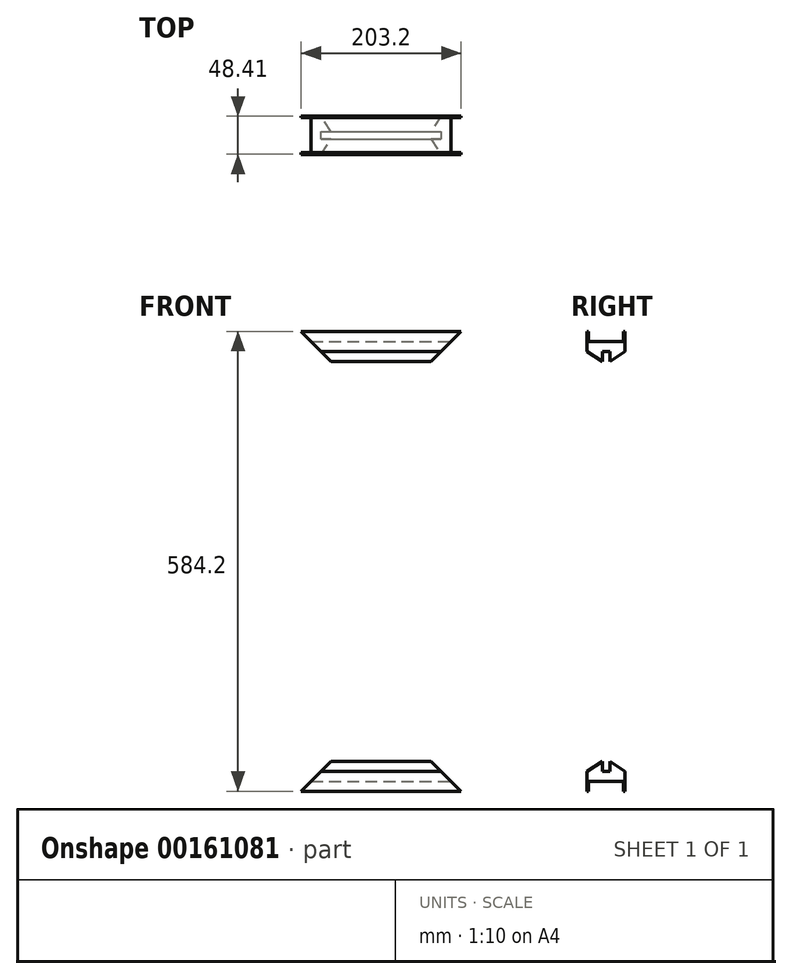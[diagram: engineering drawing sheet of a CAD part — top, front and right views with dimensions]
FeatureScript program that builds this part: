
annotation { "Feature Type Name" : "Feature", "Feature Type Description" : "" }
export const myFeature = defineFeature(function(context is Context, id is Id, definition is map)
    precondition{}
    {
        {
            var Q0;
            Q0=qCreatedBy(makeId("Top.planeOp"),FACE);
            var sketch = newSketch(context, id + "F0", { "sketchPlane" : qUnion([Q0])});
            skLineSegment(sketch, "E0.bottom", {"start": v(0, 0) * mm, "end": v(-907.26, 0) * mm});
            skLineSegment(sketch, "E0.top", {"start": v(0, 44.45) * mm, "end": v(-907.26, 44.45) * mm});
            skLineSegment(sketch, "E0.left", {"start": v(0, 0) * mm, "end": v(0, 44.45) * mm});
            skLineSegment(sketch, "E0.right", {"start": v(-907.26, 0) * mm, "end": v(-907.26, 44.45) * mm});
            skSolve(sketch);
        }
        {
            var Q0;
            Q0=qSketchRegion(id+"F0",true);
            extrude(context, id + "F1", {"entities" : qUnion([Q0]), "depth" : 2012.95 * mm});
        }
        {
            var Q0;
            Q0=qCreatedBy(makeId("Front.planeOp"),FACE);
            var sketch = newSketch(context, id + "F2", { "sketchPlane" : qUnion([Q0])});
            skPoint(sketch, "E1.0", {"position": v(0, 0) * mm});
            skLineSegment(sketch, "E2", {"start": v(0, 0) * mm, "end": v(-127, 0) * mm, "construction": true});
            skLineSegment(sketch, "E3", {"start": v(0, 0) * mm, "end": v(0, 990.6) * mm, "construction": true});
            skLineSegment(sketch, "E4.bottom", {"start": v(-127, 990.6) * mm, "end": v(-304.8, 990.6) * mm});
            skLineSegment(sketch, "E4.top", {"start": v(-127, 1549.4) * mm, "end": v(-304.8, 1549.4) * mm});
            skLineSegment(sketch, "E4.left", {"start": v(-127, 990.6) * mm, "end": v(-127, 1549.4) * mm});
            skLineSegment(sketch, "E4.right", {"start": v(-304.8, 990.6) * mm, "end": v(-304.8, 1549.4) * mm});
            skSolve(sketch);
        }
        {
            var Q0;
            Q0 = qSketchRegion(id + "F2", true);
            extrude(context, id + "F3", {"entities" : qUnion([Q0]), "operationType" : NewBodyOperationType.REMOVE, "endBound" : BoundingType.THROUGH_ALL, "oppositeDirection" : true, "depth" : 25.4 * mm});
        }
        {
            var Q0;
            Q0=qCreatedBy(makeId("Top.planeOp"),FACE);
            var sketch = newSketch(context, id + "F4", { "sketchPlane" : qUnion([Q0])});
            skLineSegment(sketch, "E5", {"start": v(-127, 44.45) * mm, "end": v(-114.3, 44.45) * mm});
            skLineSegment(sketch, "E6", {"start": v(-114.3, 44.45) * mm, "end": v(-114.3, 46.43) * mm});
            skLineSegment(sketch, "E7", {"start": v(-114.3, 46.43) * mm, "end": v(-139.7, 46.43) * mm});
            skLineSegment(sketch, "E8", {"start": v(-139.7, 46.43) * mm, "end": v(-152.4, 26.99) * mm});
            skLineSegment(sketch, "E9", {"start": v(-152.4, 26.99) * mm, "end": v(-139.7, 26.99) * mm});
            skPoint(sketch, "E10.0", {"position": v(-127, 22.23) * mm});
            skLineSegment(sketch, "E11", {"start": v(-127, 44.45) * mm, "end": v(-127, 22.23) * mm});
            skLineSegment(sketch, "E12", {"start": v(-139.7, 26.99) * mm, "end": v(-139.7, 22.23) * mm});
            skLineSegment(sketch, "E13", {"start": v(-127, 22.23) * mm, "end": v(-108.94, 22.23) * mm, "construction": true});
            skPoint(sketch, "E14.0", {"position": v(-304.8, 22.23) * mm});
            skLineSegment(sketch, "E15", {"start": v(-304.8, -29.64) * mm, "end": v(-127, -29.64) * mm, "construction": true});
            skLineSegment(sketch, "E16", {"start": v(-215.9, -29.64) * mm, "end": v(-215.9, -12.2) * mm, "construction": true});
            skLineSegment(sketch, "E17.MirrorCS", {"start": v(-127, 0) * mm, "end": v(-127, 22.23) * mm});
            skLineSegment(sketch, "E18.MirrorCS", {"start": v(-127, 0) * mm, "end": v(-114.3, 0) * mm});
            skLineSegment(sketch, "E19.MirrorCS", {"start": v(-114.3, 0) * mm, "end": v(-114.3, -1.98) * mm});
            skLineSegment(sketch, "E20.MirrorCS", {"start": v(-114.3, -1.98) * mm, "end": v(-139.7, -1.98) * mm});
            skLineSegment(sketch, "E21.MirrorCS", {"start": v(-139.7, -1.98) * mm, "end": v(-152.4, 17.46) * mm});
            skLineSegment(sketch, "E22.MirrorCS", {"start": v(-152.4, 17.46) * mm, "end": v(-139.7, 17.46) * mm});
            skLineSegment(sketch, "E23.MirrorCS", {"start": v(-139.7, 17.46) * mm, "end": v(-139.7, 22.23) * mm});
            skLineSegment(sketch, "E24.MirrorCS", {"start": v(-317.5, 44.45) * mm, "end": v(-317.5, 46.43) * mm});
            skLineSegment(sketch, "E25.MirrorCS", {"start": v(-292.1, 17.46) * mm, "end": v(-292.1, 22.23) * mm});
            skLineSegment(sketch, "E26.MirrorCS", {"start": v(-292.1, 26.99) * mm, "end": v(-292.1, 22.23) * mm});
            skLineSegment(sketch, "E27.MirrorCS", {"start": v(-317.5, 0) * mm, "end": v(-317.5, -1.98) * mm});
            skLineSegment(sketch, "E28.MirrorCS", {"start": v(-304.8, 44.45) * mm, "end": v(-317.5, 44.45) * mm});
            skLineSegment(sketch, "E29.MirrorCS", {"start": v(-279.4, 17.46) * mm, "end": v(-292.1, 17.46) * mm});
            skLineSegment(sketch, "E30.MirrorCS", {"start": v(-304.8, 0) * mm, "end": v(-317.5, 0) * mm});
            skLineSegment(sketch, "E31.MirrorCS", {"start": v(-292.1, -1.98) * mm, "end": v(-279.4, 17.46) * mm});
            skLineSegment(sketch, "E32.MirrorCS", {"start": v(-317.5, 46.43) * mm, "end": v(-292.1, 46.43) * mm});
            skLineSegment(sketch, "E33.MirrorCS", {"start": v(-292.1, 46.43) * mm, "end": v(-279.4, 26.99) * mm});
            skLineSegment(sketch, "E34.MirrorCS", {"start": v(-317.5, -1.98) * mm, "end": v(-292.1, -1.98) * mm});
            skLineSegment(sketch, "E35.MirrorCS", {"start": v(-304.8, 44.45) * mm, "end": v(-304.8, 22.23) * mm});
            skLineSegment(sketch, "E36.MirrorCS", {"start": v(-304.8, 0) * mm, "end": v(-304.8, 22.23) * mm});
            skLineSegment(sketch, "E37.MirrorCS", {"start": v(-279.4, 26.99) * mm, "end": v(-292.1, 26.99) * mm});
            skSolve(sketch);
        }
        {
            var Q0;
            Q0=qCreatedBy(makeId("Front.planeOp"),FACE);
            var sketch = newSketch(context, id + "F5", { "sketchPlane" : qUnion([Q0])});
            skPoint(sketch, "E38.0", {"position": v(-304.8, 1549.4) * mm});
            skPoint(sketch, "E39.0", {"position": v(-127, 1549.4) * mm});
            skPoint(sketch, "E40.0", {"position": v(-127, 990.6) * mm});
            skPoint(sketch, "E41.0", {"position": v(-304.8, 990.6) * mm});
            skLineSegment(sketch, "E42", {"start": v(-127, 1549.4) * mm, "end": v(-215.9, 1460.5) * mm});
            skLineSegment(sketch, "E43", {"start": v(-215.9, 1460.5) * mm, "end": v(-304.8, 1549.4) * mm});
            skLineSegment(sketch, "E44", {"start": v(-304.8, 1549.4) * mm, "end": v(-768.35, 2012.95) * mm});
            skLineSegment(sketch, "E45", {"start": v(-127, 1549.4) * mm, "end": v(336.55, 2012.95) * mm});
            skLineSegment(sketch, "E46", {"start": v(-768.35, 2012.95) * mm, "end": v(336.55, 2012.95) * mm});
            skLineSegment(sketch, "E47", {"start": v(162.14, 1549.4) * mm, "end": v(162.14, 990.6) * mm, "construction": true});
            skLineSegment(sketch, "E48", {"start": v(162.14, 1270) * mm, "end": v(365.55, 1270) * mm, "construction": true});
            skPoint(sketch, "E48.endSnap0", {"position": v(162.14, 1270) * mm});
            skLineSegment(sketch, "E49.MirrorCS", {"start": v(-215.9, 1079.5) * mm, "end": v(-304.8, 990.6) * mm});
            skLineSegment(sketch, "E50.MirrorCS", {"start": v(-127, 990.6) * mm, "end": v(-215.9, 1079.5) * mm});
            skLineSegment(sketch, "E51", {"start": v(-304.8, 990.6) * mm, "end": v(-1295.4, 0) * mm});
            skLineSegment(sketch, "E52", {"start": v(-1295.4, 0) * mm, "end": v(863.6, 0) * mm});
            skLineSegment(sketch, "E53", {"start": v(863.6, 0) * mm, "end": v(-127, 990.6) * mm});
            skSolve(sketch);
        }
        {
            var Q0;
            Q0=qCreatedBy(makeId("Front.planeOp"),FACE);
            var sketch = newSketch(context, id + "F6", { "sketchPlane" : qUnion([Q0])});
            skLineSegment(sketch, "E54.0", {"start": v(-215.9, 1460.5) * mm, "end": v(-304.8, 1549.4) * mm});
            skLineSegment(sketch, "E55.0", {"start": v(-127, 1549.4) * mm, "end": v(-215.9, 1460.5) * mm});
            skLineSegment(sketch, "E56.0", {"start": v(-127, 990.6) * mm, "end": v(-215.9, 1079.5) * mm});
            skLineSegment(sketch, "E57.0", {"start": v(-215.9, 1079.5) * mm, "end": v(-304.8, 990.6) * mm});
            skLineSegment(sketch, "E58", {"start": v(-304.8, 1549.4) * mm, "end": v(-907.26, 2151.86) * mm});
            skLineSegment(sketch, "E59", {"start": v(0, 1676.4) * mm, "end": v(-127, 1549.4) * mm});
            skLineSegment(sketch, "E60.0", {"start": v(162.14, 1270) * mm, "end": v(365.55, 1270) * mm, "construction": true});
            skLineSegment(sketch, "E61.MirrorCS", {"start": v(0, 863.6) * mm, "end": v(-127, 990.6) * mm});
            skLineSegment(sketch, "E62.MirrorCS", {"start": v(-304.8, 990.6) * mm, "end": v(-907.26, 388.14) * mm});
            skLineSegment(sketch, "E63", {"start": v(-907.26, 2151.86) * mm, "end": v(-907.26, 388.14) * mm});
            skLineSegment(sketch, "E64", {"start": v(0, 1676.4) * mm, "end": v(0, 863.6) * mm});
            skSolve(sketch);
        }
        {
            var Q0;
            Q0 = qSketchRegion(id + "F4", true);
            var Q1;
            Q1=makeQuery(id+"F1.opExtrude","CAP_FACE",FACE,{"disambiguationData":[OSD([sQuery(id+"F0.wireOp",EDGE,"E0.bottom"),sQuery(id+"F0.wireOp",EDGE,"E0.top"),sQuery(id+"F0.wireOp",EDGE,"E0.left"),sQuery(id+"F0.wireOp",EDGE,"E0.right")])],"isStart":false});
            extrude(context, id + "F7", {"entities" : qUnion([Q0]), "endBound" : BoundingType.UP_TO_SURFACE, "endBoundEntityFace" : qUnion([Q1]), "depth" : 25.4 * mm});
        }
        {
            var Q0;
            Q0 = qSketchRegion(id + "F5", true);
            extrude(context, id + "F8", {"entities" : qUnion([Q0]), "operationType" : NewBodyOperationType.REMOVE, "endBound" : BoundingType.THROUGH_ALL, "oppositeDirection" : true, "depth" : 25.4 * mm, "hasSecondDirection" : true, "secondDirectionBound" : SecondDirectionBoundingType.THROUGH_ALL, "secondDirectionOppositeDirection" : false, "secondDirectionDepth" : 25.4 * mm});
        }
        {
            var Q0;
            Q0=qCreatedBy(makeId("Right.planeOp"),FACE);
            var sketch = newSketch(context, id + "F9", { "sketchPlane" : qUnion([Q0])});
            skLineSegment(sketch, "E65.0.0", {"start": v(17.46, 1536.7) * mm, "end": v(17.46, 1524) * mm});
            skLineSegment(sketch, "E65.0.1", {"start": v(17.46, 1524) * mm, "end": v(-1.98, 1536.7) * mm});
            skLineSegment(sketch, "E65.0.2", {"start": v(-1.98, 1536.7) * mm, "end": v(-1.98, 1562.1) * mm});
            skLineSegment(sketch, "E65.0.3", {"start": v(-1.98, 1562.1) * mm, "end": v(0, 1562.1) * mm});
            skLineSegment(sketch, "E65.0.4", {"start": v(0, 1562.1) * mm, "end": v(0, 1549.4) * mm});
            skLineSegment(sketch, "E65.0.5", {"start": v(0, 1549.4) * mm, "end": v(44.45, 1549.4) * mm});
            skLineSegment(sketch, "E65.0.6", {"start": v(44.45, 1549.4) * mm, "end": v(44.45, 1562.1) * mm});
            skLineSegment(sketch, "E65.0.7", {"start": v(44.45, 1562.1) * mm, "end": v(46.43, 1562.1) * mm});
            skLineSegment(sketch, "E65.0.8", {"start": v(46.43, 1562.1) * mm, "end": v(46.43, 1536.7) * mm});
            skLineSegment(sketch, "E65.0.9", {"start": v(46.43, 1536.7) * mm, "end": v(26.99, 1524) * mm});
            skLineSegment(sketch, "E65.0.10", {"start": v(26.99, 1524) * mm, "end": v(26.99, 1536.7) * mm});
            skLineSegment(sketch, "E65.0.11", {"start": v(26.99, 1536.7) * mm, "end": v(17.46, 1536.7) * mm});
            skLineSegment(sketch, "E66.0.0", {"start": v(17.46, 1003.3) * mm, "end": v(26.99, 1003.3) * mm});
            skLineSegment(sketch, "E66.0.1", {"start": v(26.99, 1003.3) * mm, "end": v(26.99, 1016) * mm});
            skLineSegment(sketch, "E66.0.2", {"start": v(26.99, 1016) * mm, "end": v(46.43, 1003.3) * mm});
            skLineSegment(sketch, "E66.0.3", {"start": v(46.43, 1003.3) * mm, "end": v(46.43, 977.9) * mm});
            skLineSegment(sketch, "E66.0.4", {"start": v(46.43, 977.9) * mm, "end": v(44.45, 977.9) * mm});
            skLineSegment(sketch, "E66.0.5", {"start": v(44.45, 977.9) * mm, "end": v(44.45, 990.6) * mm});
            skLineSegment(sketch, "E66.0.6", {"start": v(44.45, 990.6) * mm, "end": v(0, 990.6) * mm});
            skLineSegment(sketch, "E66.0.7", {"start": v(0, 990.6) * mm, "end": v(0, 977.9) * mm});
            skLineSegment(sketch, "E66.0.8", {"start": v(0, 977.9) * mm, "end": v(-1.98, 977.9) * mm});
            skLineSegment(sketch, "E66.0.9", {"start": v(-1.98, 977.9) * mm, "end": v(-1.98, 1003.3) * mm});
            skLineSegment(sketch, "E66.0.10", {"start": v(-1.98, 1003.3) * mm, "end": v(17.46, 1016) * mm});
            skLineSegment(sketch, "E66.0.11", {"start": v(17.46, 1016) * mm, "end": v(17.46, 1003.3) * mm});
            skSolve(sketch);
        }
        {
            var Q0;
            Q0 = qSketchRegion(id + "F9", true);
            var Q1;
            Q1=makeQuery(id+"F1.opExtrude","SWEPT_FACE",FACE,{"disambiguationData":[OSD([sQuery(id+"F0.wireOp",EDGE,"E0.right")])]});
            extrude(context, id + "F10", {"entities" : qUnion([Q0]), "endBound" : BoundingType.UP_TO_SURFACE, "oppositeDirection" : true, "endBoundEntityFace" : qUnion([Q1]), "depth" : 25.4 * mm});
        }
        {
            var Q0;
            Q0 = qSketchRegion(id + "F6", true);
            extrude(context, id + "F11", {"entities" : qUnion([Q0]), "operationType" : NewBodyOperationType.REMOVE, "endBound" : BoundingType.THROUGH_ALL, "oppositeDirection" : true, "depth" : 25.4 * mm, "hasSecondDirection" : true, "secondDirectionBound" : SecondDirectionBoundingType.THROUGH_ALL, "secondDirectionOppositeDirection" : false, "secondDirectionDepth" : 25.4 * mm});
        }
    });
